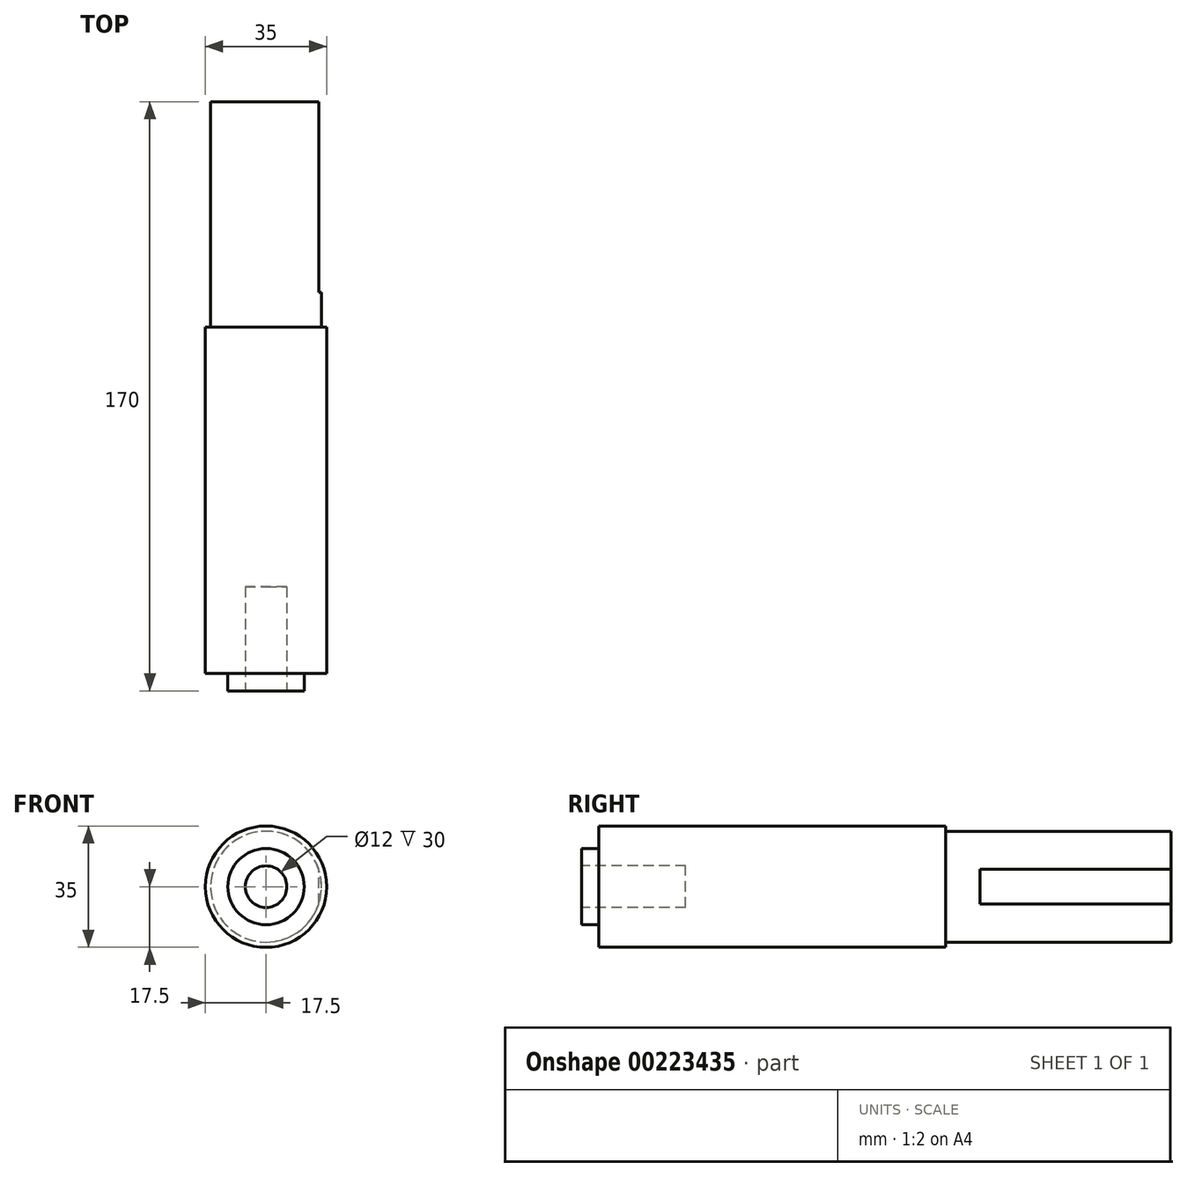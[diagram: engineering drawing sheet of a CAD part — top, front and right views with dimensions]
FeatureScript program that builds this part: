
annotation { "Feature Type Name" : "Feature", "Feature Type Description" : "" }
export const myFeature = defineFeature(function(context is Context, id is Id, definition is map)
    precondition{}
    {
        {
            var Q0;
            Q0=qCreatedBy(makeId("Front.planeOp"),FACE);
            var sketch = newSketch(context, id + "F0", { "sketchPlane" : qUnion([Q0])});
            skCircle(sketch, "E0", {"center": v(0, 0) * mm, "radius": 17.5 * mm});
            skSolve(sketch);
        }
        {
            var Q0;
            Q0=makeQuery(id+"F0.imprint","IMPRINT",FACE,{"disambiguationData":[TD([[makeQuery(id+"F0.imprint","IMPRINT",EDGE,{"derivedFrom":sQuery(id+"F0.wireOp",EDGE,"E0")}),1.0]])]});
            extrude(context, id + "F1", {"entities" : qUnion([Q0]), "depth" : 100 * mm});
        }
        {
            var Q0;
            Q0=makeQuery(id+"F1.opExtrude","CAP_FACE",FACE,{"disambiguationData":[OSD([sQuery(id+"F0.wireOp",EDGE,"E0")])],"isStart":false});
            var sketch = newSketch(context, id + "F2", { "sketchPlane" : qUnion([Q0])});
            skCircle(sketch, "E1", {"center": v(0, 0) * mm, "radius": 11 * mm});
            skSolve(sketch);
        }
        {
            var Q0;
            Q0 = qSketchRegion(id + "F2", true);
            extrude(context, id + "F3", {"entities" : qUnion([Q0]), "operationType" : NewBodyOperationType.ADD, "depth" : 5 * mm});
        }
        {
            var Q0;
            Q0=makeQuery(id+"F3.opExtrude","CAP_FACE",FACE,{"disambiguationData":[OSD([sQuery(id+"F2.wireOp",EDGE,"E1")])],"isStart":false});
            var sketch = newSketch(context, id + "F4", { "sketchPlane" : qUnion([Q0])});
            skCircle(sketch, "E2", {"center": v(0, 0) * mm, "radius": 6 * mm});
            skSolve(sketch);
        }
        {
            var Q0;
            Q0 = qSketchRegion(id + "F4", true);
            extrude(context, id + "F5", {"entities" : qUnion([Q0]), "operationType" : NewBodyOperationType.REMOVE, "oppositeDirection" : true, "depth" : 30 * mm});
        }
        {
            var Q0;
            Q0=qCreatedBy(makeId("Front.planeOp"),FACE);
            var sketch = newSketch(context, id + "F6", { "sketchPlane" : qUnion([Q0])});
            skCircle(sketch, "E3", {"center": v(0, 0) * mm, "radius": 16 * mm});
            skSolve(sketch);
        }
        {
            var Q0;
            Q0=makeQuery(id+"F6.imprint","IMPRINT",FACE,{"disambiguationData":[TD([[makeQuery(id+"F6.imprint","IMPRINT",EDGE,{"derivedFrom":sQuery(id+"F6.wireOp",EDGE,"E3")}),1.0]])]});
            extrude(context, id + "F7", {"entities" : qUnion([Q0]), "operationType" : NewBodyOperationType.ADD, "oppositeDirection" : true, "depth" : 65 * mm});
        }
        {
            var Q0;
            Q0=makeQuery(id+"F7.opExtrude","CAP_FACE",FACE,{"disambiguationData":[OSD([sQuery(id+"F6.wireOp",EDGE,"E3")])],"isStart":false});
            var sketch = newSketch(context, id + "F8", { "sketchPlane" : qUnion([Q0])});
            skLineSegment(sketch, "E4", {"start": v(0, 0) * mm, "end": v(-0.7, 0) * mm});
            skLineSegment(sketch, "E5.0", {"start": v(-20.85, -5) * mm, "end": v(-15.2, -5) * mm});
            skLineSegment(sketch, "E6.0", {"start": v(-20.85, 5) * mm, "end": v(-15.2, 5) * mm});
            skLineSegment(sketch, "E7", {"start": v(-15.2, -5) * mm, "end": v(-15.2, 5) * mm});
            skLineSegment(sketch, "E8.trimOffspring", {"start": v(-0.7, 0) * mm, "end": v(0, 0) * mm});
            skPoint(sketch, "E9.start.orphan", {"position": v(-20.85, 0) * mm});
            skLineSegment(sketch, "E10", {"start": v(-20.85, -5) * mm, "end": v(-20.85, 5) * mm});
            skSolve(sketch);
        }
        {
            var Q0;
            Q0 = qSketchRegion(id + "F8", true);
            extrude(context, id + "F9", {"entities" : qUnion([Q0]), "operationType" : NewBodyOperationType.REMOVE, "oppositeDirection" : true, "depth" : 55 * mm});
        }
    });
